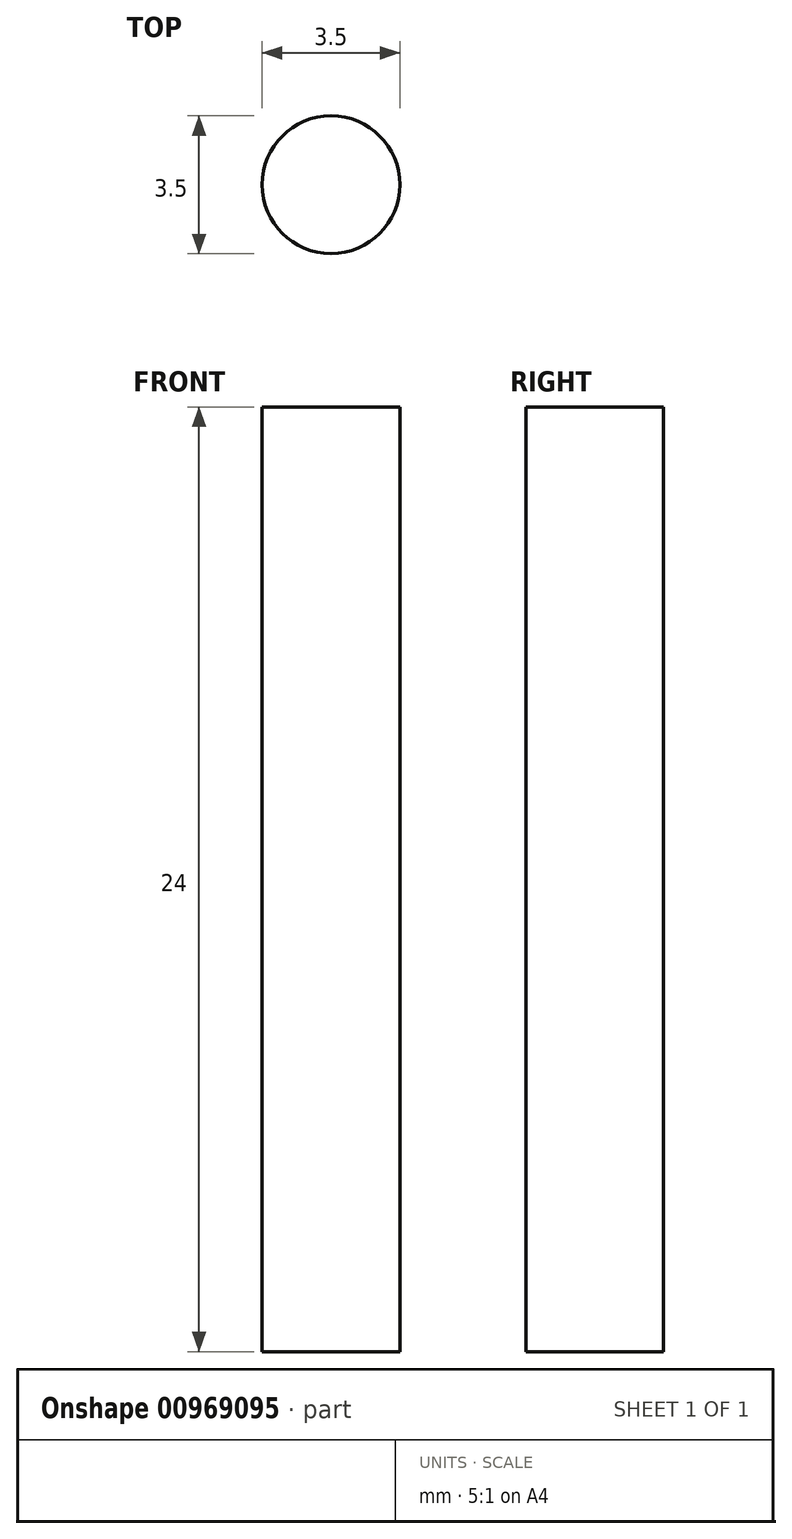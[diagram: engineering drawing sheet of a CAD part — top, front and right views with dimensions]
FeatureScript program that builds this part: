
annotation { "Feature Type Name" : "Feature", "Feature Type Description" : "" }
export const myFeature = defineFeature(function(context is Context, id is Id, definition is map)
    precondition{}
    {
        {
            var Q0;
            Q0=qCreatedBy(makeId("Top.planeOp"),FACE);
            var sketch = newSketch(context, id + "F0", { "sketchPlane" : qUnion([Q0])});
            skCircle(sketch, "E0", {"center": v(0, 0) * mm, "radius": 1.75 * mm});
            skSolve(sketch);
        }
        {
            var Q0;
            Q0=makeQuery(id+"F0.imprint","IMPRINT",FACE,{"disambiguationData":[TD([[makeQuery(id+"F0.imprint","IMPRINT",EDGE,{"derivedFrom":sQuery(id+"F0.wireOp",EDGE,"E0")}),1.0]])]});
            extrude(context, id + "F1", {"entities" : qUnion([Q0]), "depth" : 24 * mm, "offsetDistance" : 25 * mm});
        }
    });
